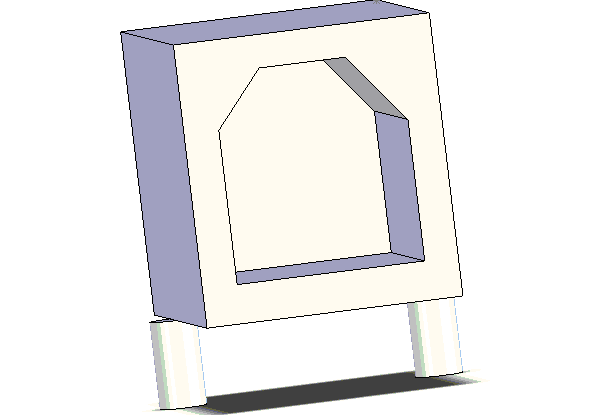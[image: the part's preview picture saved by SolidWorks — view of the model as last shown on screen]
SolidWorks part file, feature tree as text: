
SOLIDWORKS PART (.sldprt)
format: sldprt  version: not decoded by parser v0  size: 111,104 bytes
history: native  units: mm
features: sketch x3, extrude x2, cut_extrude x1 (+11 scaffold rows collapsed)
feature tree (17):
  scaffold x11  (default folders/planes/origin — collapsed)
  sketch  "Sketch1"  dims[D1=16.002mm D2=12.0396mm]
  extrude  "Extrude1"  Depth=10.9728mm
  sketch  "Sketch2"  dims[D1=2.032mm D2=2.032mm D3=10.287mm D4=10.287mm]
  extrude  "Extrude2"  Depth=3.7084mm
  sketch  "Sketch3"
  cut_extrude  "Cut-Extrude1"  Depth=10.16mm
decode coverage: 5 of 6 modeling features carry decoded parameters
note: suppression state not decoded; provenance and decode notes live in map.json
